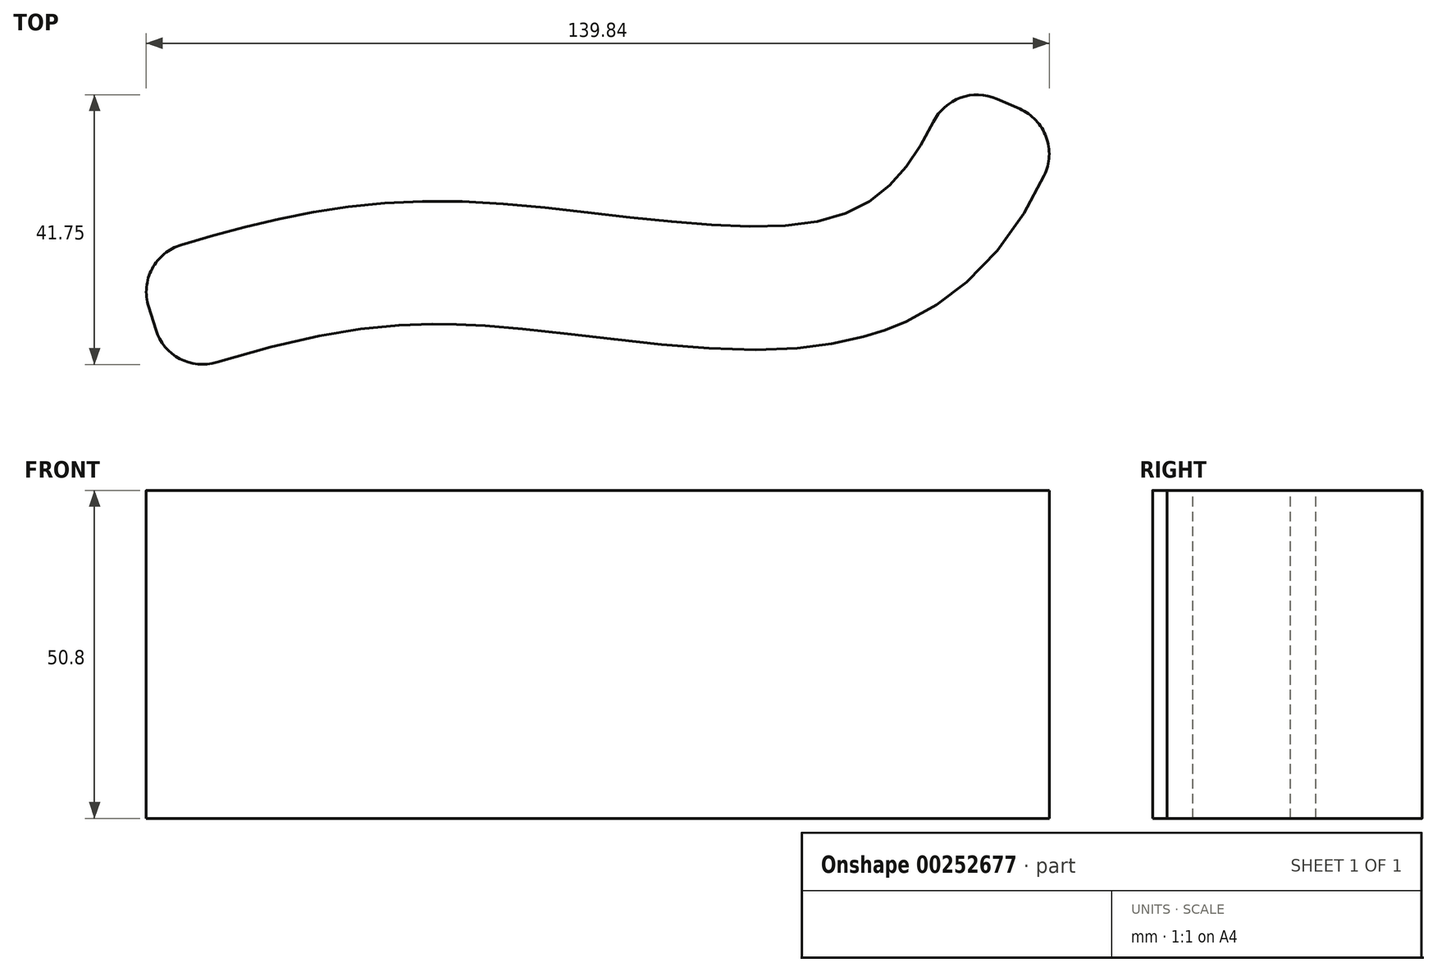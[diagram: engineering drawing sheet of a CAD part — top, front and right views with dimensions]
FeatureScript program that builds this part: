
annotation { "Feature Type Name" : "Feature", "Feature Type Description" : "" }
export const myFeature = defineFeature(function(context is Context, id is Id, definition is map)
    precondition{}
    {
        {
            var Q0;
            Q0=qCreatedBy(makeId("Top.planeOp"),FACE);
            var sketch = newSketch(context, id + "F0", { "sketchPlane" : qUnion([Q0])});
            skFitSpline(sketch, "E0", {"points": [v(-60.94, 25.06) * mm, v(-11.46, 34.06) * mm, v(49.16, 32.13) * mm, v(65.87, 52.91) * mm], "startDerivative": vector(128.58, 39.95) * mm, "endDerivative": vector(44.22, 100.9) * mm});
            skFitSpline(sketch, "E1.0", {"points": [v(-55.3, 6.87) * mm, v(-52.61, 7.7) * mm, v(-47.4, 9.32) * mm, v(-39.88, 11.46) * mm, v(-33.73, 12.9) * mm, v(-28.79, 13.81) * mm, v(-25.04, 14.36) * mm, v(-21.22, 14.76) * mm, v(-17.96, 14.96) * mm, v(-15.28, 15.03) * mm, v(-13.57, 15.04) * mm, v(-12.19, 15.02) * mm, v(-10.79, 14.99) * mm, v(-8.96, 14.91) * mm, v(-6.67, 14.78) * mm, v(-3.5, 14.54) * mm, v(0.64, 14.14) * mm, v(5.84, 13.57) * mm, v(11.21, 12.94) * mm, v(16.7, 12.31) * mm, v(22.26, 11.75) * mm, v(27.87, 11.31) * mm, v(33.54, 11.07) * mm, v(38.31, 11.12) * mm, v(42.19, 11.36) * mm, v(45.14, 11.67) * mm, v(48.13, 12.14) * mm, v(50.67, 12.7) * mm, v(52.73, 13.25) * mm, v(54.03, 13.65) * mm, v(55.08, 14) * mm, v(55.87, 14.3) * mm, v(56.65, 14.6) * mm, v(58.2, 15.25) * mm, v(60.46, 16.32) * mm, v(63.28, 17.98) * mm, v(65.88, 19.8) * mm, v(69.04, 22.43) * mm, v(72.41, 25.94) * mm, v(75.6, 30.21) * mm, v(78.14, 34.37) * mm, v(80.18, 38.32) * mm, v(81.88, 41.99) * mm, v(82.86, 44.21) * mm, v(83.32, 45.27) * mm]});
            skLineSegment(sketch, "E2", {"start": v(-60.94, 25.06) * mm, "end": v(-55.3, 6.87) * mm});
            skLineSegment(sketch, "E3", {"start": v(65.87, 52.91) * mm, "end": v(83.32, 45.27) * mm});
            skSolve(sketch);
        }
        {
            var Q0;
            Q0=makeQuery(id+"F0.imprint","IMPRINT",FACE,{"disambiguationData":[TD([[makeQuery(id+"F0.imprint","IMPRINT",EDGE,{"derivedFrom":sQuery(id+"F0.wireOp",EDGE,"E0")}),-1.0]])]});
            extrude(context, id + "F1", {"entities" : qUnion([Q0]), "depth" : 50.8 * mm});
        }
        {
            var Q0;
            Q0=makeQuery(id+"F1.opExtrude","SWEPT_EDGE",EDGE,{"disambiguationData":[OSD([sQuery(id+"F0.wireOp",EDGE,"E0"),sQuery(id+"F0.wireOp",EDGE,"E3")])]});
            var Q1;
            Q1=makeQuery(id+"F1.opExtrude","SWEPT_EDGE",EDGE,{"disambiguationData":[OSD([sQuery(id+"F0.wireOp",EDGE,"E1.0"),sQuery(id+"F0.wireOp",EDGE,"E3")])]});
            var Q2;
            Q2=makeQuery(id+"F1.opExtrude","SWEPT_EDGE",EDGE,{"disambiguationData":[OSD([sQuery(id+"F0.wireOp",EDGE,"E0"),sQuery(id+"F0.wireOp",EDGE,"E2")])]});
            var Q3;
            Q3=makeQuery(id+"F1.opExtrude","SWEPT_EDGE",EDGE,{"disambiguationData":[OSD([sQuery(id+"F0.wireOp",EDGE,"E1.0"),sQuery(id+"F0.wireOp",EDGE,"E2")])]});
            fillet(context, id + "F2", {"entities" : qUnion([Q0, Q1, Q2, Q3]), "radius" : 7.62 * mm, "tangentPropagation" : true, "allowEdgeOverflow" : false});
        }
    });
